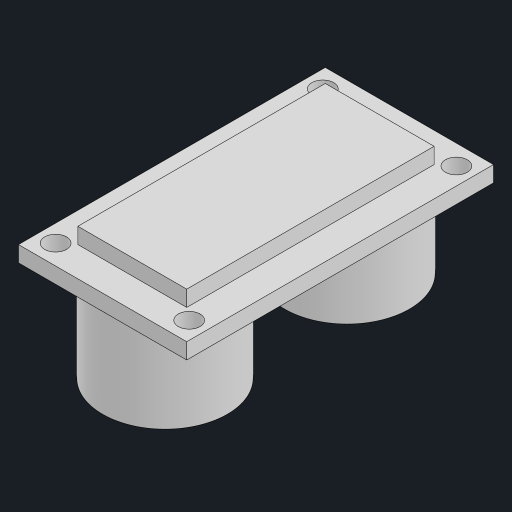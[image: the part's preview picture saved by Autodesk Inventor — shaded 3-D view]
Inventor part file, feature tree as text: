
AUTODESK INVENTOR PART (.ipt)
format: ipt  version: 2023 (Build 270158000, 158)  size: 136,192 bytes
history: native  units: mm
features: extrude x3, sketch x2, other x1
ambient origin geometry x8: Origin, YZ Plane, XZ Plane, XY Plane, X Axis, Y Axis, Z Axis, Center Point
bodies: Body1 (feature_tree)
feature tree (6):
  other  "ソリッド1"
  sketch  "スケッチ1"
  extrude  "押し出し1"  Depth=17.0mm
  extrude  "押し出し2"  Depth=31.0mm
  extrude  "押し出し3"  Depth=12.6mm
  sketch  "スケッチ2"
